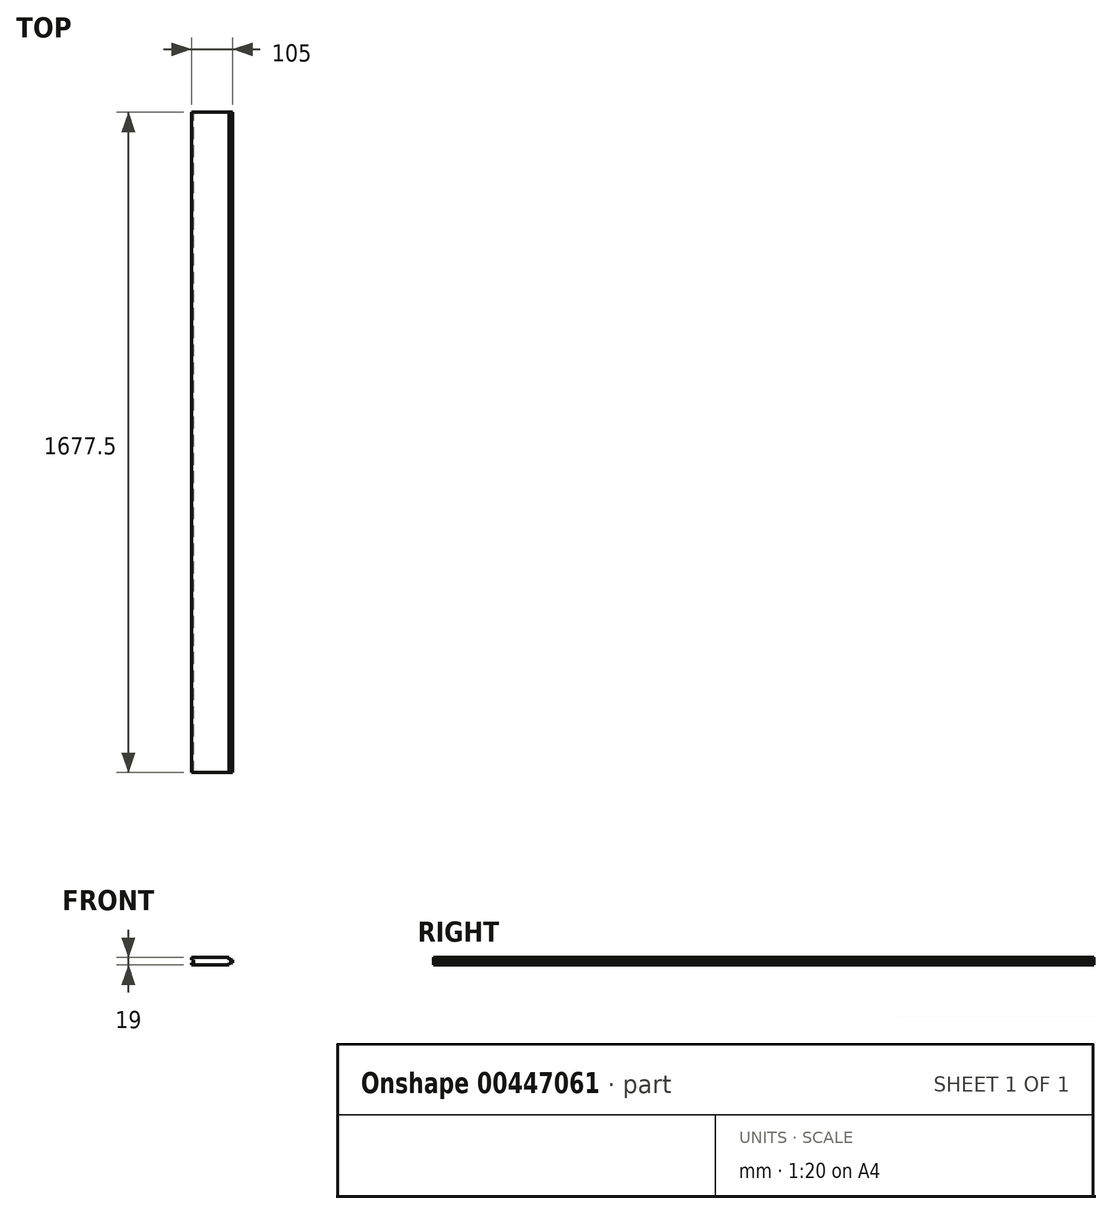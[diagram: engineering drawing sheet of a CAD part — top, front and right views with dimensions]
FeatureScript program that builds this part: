
annotation { "Feature Type Name" : "Feature", "Feature Type Description" : "" }
export const myFeature = defineFeature(function(context is Context, id is Id, definition is map)
    precondition{}
    {
        {
            var Q0;
            Q0=qCreatedBy(makeId("Front.planeOp"),FACE);
            var sketch = newSketch(context, id + "F0", { "sketchPlane" : qUnion([Q0])});
            skLineSegment(sketch, "E0", {"start": v(0, 0) * mm, "end": v(0, 6) * mm});
            skLineSegment(sketch, "E1", {"start": v(0, 6) * mm, "end": v(5, 6) * mm});
            skLineSegment(sketch, "E2", {"start": v(5, 6) * mm, "end": v(5, 13) * mm});
            skLineSegment(sketch, "E3", {"start": v(5, 13) * mm, "end": v(0, 13) * mm});
            skLineSegment(sketch, "E4", {"start": v(0, 13) * mm, "end": v(0, 19) * mm});
            skLineSegment(sketch, "E5", {"start": v(0, 19) * mm, "end": v(96, 19) * mm});
            skLineSegment(sketch, "E6", {"start": v(96, 19) * mm, "end": v(96, 13) * mm});
            skLineSegment(sketch, "E7", {"start": v(96, 13) * mm, "end": v(105, 13) * mm});
            skLineSegment(sketch, "E8", {"start": v(105, 13) * mm, "end": v(105, 6) * mm});
            skLineSegment(sketch, "E9", {"start": v(105, 6) * mm, "end": v(96, 6) * mm});
            skLineSegment(sketch, "E10", {"start": v(96, 6) * mm, "end": v(96, 0) * mm});
            skLineSegment(sketch, "E11", {"start": v(96, 0) * mm, "end": v(0, 0) * mm});
            skSolve(sketch);
        }
        {
            var Q0;
            Q0=makeQuery(id+"F0.imprint","IMPRINT",FACE,{"disambiguationData":[TD([[makeQuery(id+"F0.imprint","IMPRINT",EDGE,{"derivedFrom":sQuery(id+"F0.wireOp",EDGE,"E0")}),-1.0]])]});
            extrude(context, id + "F1", {"entities" : qUnion([Q0]), "depth" : (1477.5 + 200) * mm, "offsetDistance" : 25 * mm});
        }
        {
            var Q0;
            Q0=makeQuery(id+"F0.imprint","IMPRINT",FACE,{"disambiguationData":[TD([[makeQuery(id+"F0.imprint","IMPRINT",EDGE,{"derivedFrom":sQuery(id+"F0.wireOp",EDGE,"E0")}),-1.0]])]});
            extrude(context, id + "F2", {"entities" : qUnion([Q0]), "depth" : (1477.5 + 200) * mm, "offsetDistance" : 25 * mm});
        }
    });
